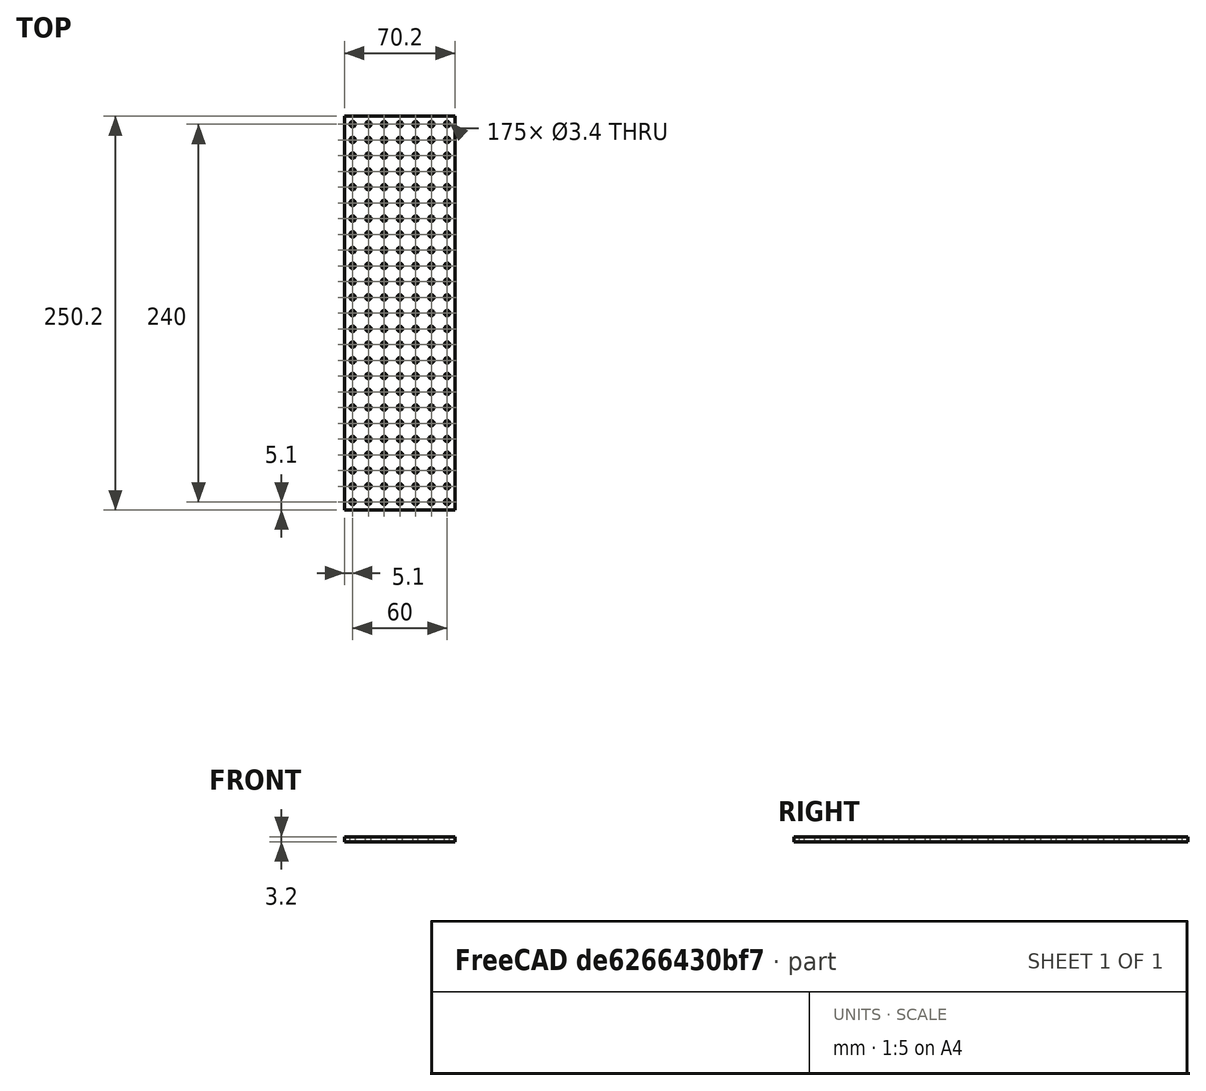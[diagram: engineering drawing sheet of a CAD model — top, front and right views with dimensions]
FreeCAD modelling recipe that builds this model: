
FCSTD DOCUMENT  (FreeCAD 0.20R29410 (Git))
Label: hole_plate3
License: All rights reserved
LicenseURL: http://en.wikipedia.org/wiki/All_rights_reserved
objects: Spreadsheet::Sheet×1, Part::Box×1, Part::Cylinder×1, Part::FeaturePython×1, Part::Cut×1, App::Part×1, TechDraw::DrawSVGTemplate×1, Part::Offset×1, App::DocumentObjectGroup×1, TechDraw::DrawViewPart×1, TechDraw::DrawPage×1
note: 5 computed .brp shape members not serialized (recipe doc carries the construction recipe); baked Part::Feature solids carry a one-line shape summary decoded from their .brp

FEATURE [Spreadsheet::Sheet] Spreadsheet  label="p"
  cells = A1=hole_r; B1(hole_r)=1.8; A2=plate_hole_dist; B2(plate_hole_dist)=10; A3=plate_x; B3(plate_x)=250; A4=plate_y; B4(plate_y)=70
FEATURE [Part::Box] Box  label="hole plate cube"
  AttacherType = Attacher::AttachEngine3D
  Height = 3
  Length = 250
  Width = 70
  expr: Length = <<p>>.plate_x
  expr: Width = <<p>>.plate_y
FEATURE [Part::Cylinder] Cylinder  label="the hole"
  Angle = 360
  AttacherType = Attacher::AttachEngine3D
  FirstAngle = 0
  Height = 10
  Radius = 1.8
  SecondAngle = 0
  expr: Radius = <<p>>.hole_r
FEATURE [Part::FeaturePython] Array  label="hole array"  # Draft array (typed FeaturePython)
  Angle = 360
  ArrayType = 0
  Axis = (0,0,1)
  Base = -> Cylinder
  Center = (0,0,0)
  Fuse = false
  IntervalAxis = (0,0,0)
  IntervalX = (10,0,0)
  IntervalY = (0,10,0)
  IntervalZ = (0,0,1)
  NumberPolar = 1
  NumberX = 25
  NumberY = 7
  NumberZ = 1
  Placement = pos=(5,5,0) rot=(0,0,1;0rad)
  expr: .IntervalX.x = <<p>>.plate_hole_dist
  expr: .Placement.Base.x = <<p>>.plate_hole_dist / 2
  expr: .Placement.Base.y = <<p>>.plate_hole_dist / 2
  expr: NumberX = floor(<<p>>.plate_x / <<p>>.plate_hole_dist)
  expr: NumberY = floor(<<p>>.plate_y / <<p>>.plate_hole_dist)
FEATURE [Part::Cut] Cut  label="hole plate cut"
  Base = -> Box
  Tool = -> Array
FEATURE [App::Part] Part
  Group = -> [Cut]
  Origin = -> Origin
FEATURE [TechDraw::DrawSVGTemplate] Template
  Height = 250.4
  Orientation = 0
  Width = 70.6
FEATURE [Part::Offset] hole_plate_cut_offset
  Fill = false
  Intersection = false
  Join = 2
  Mode = 0
  Placement = pos=(-0.2,0.2,0) rot=(0,0,1;1.5708rad)
  SelfIntersection = false
  Source = -> Cut
  Value = 0.1
FEATURE [App::DocumentObjectGroup] LaserCutterExportObjects
  Group = -> [hole_plate_cut_offset]
FEATURE [TechDraw::DrawViewPart] hole_plate_cut_contour
  CoarseView = true
  Direction = (0,0,1)
  Focus = 100
  HardHidden = false
  IsoCount = 0
  IsoHidden = false
  IsoVisible = false
  LockPosition = false
  Perspective = false
  Rotation = 0
  ScaleType = 2
  SeamHidden = false
  SeamVisible = true
  SmoothHidden = false
  SmoothVisible = true
  Source = -> [hole_plate_cut_offset]
  X = 35.3
  XDirection = (1,0,0)
  Y = 125.1
FEATURE [TechDraw::DrawPage] LaserCutterExport
  KeepUpdated = true
  NextBalloonIndex = 1
  ProjectionType = 0
  Template = -> Template
  Views = -> [hole_plate_cut_contour]
